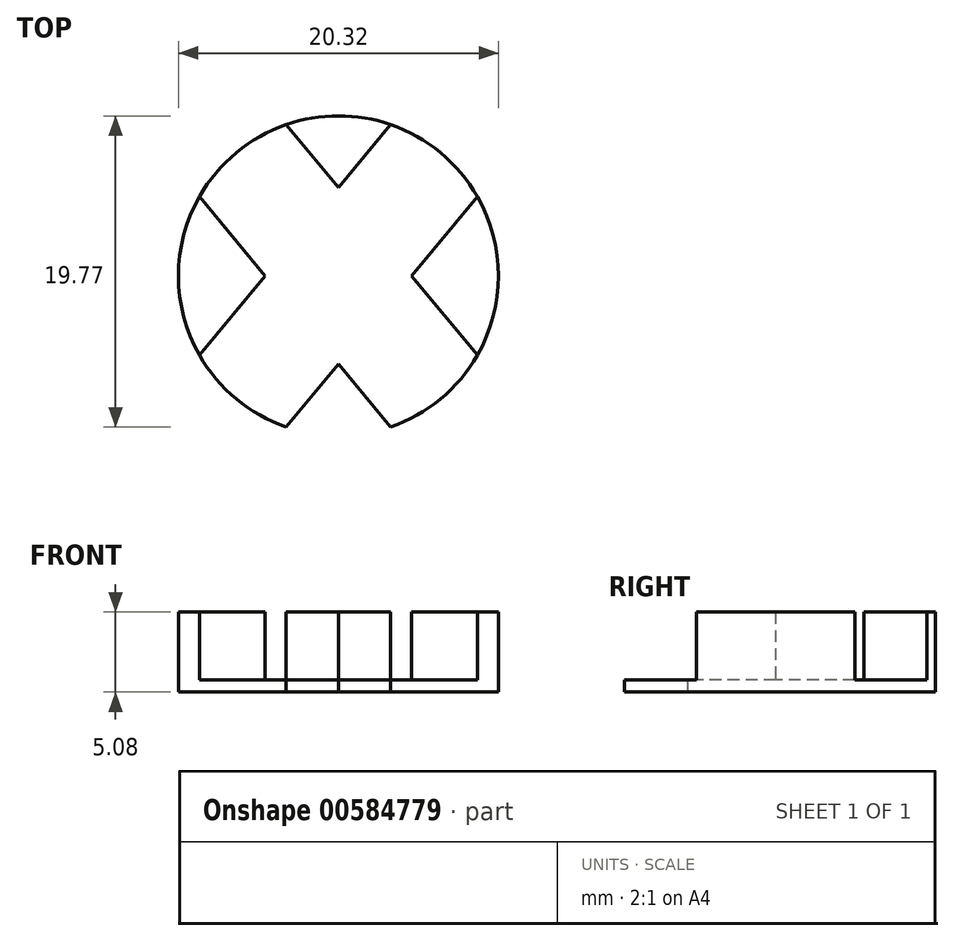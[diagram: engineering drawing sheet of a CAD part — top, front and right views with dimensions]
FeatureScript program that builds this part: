
annotation { "Feature Type Name" : "Feature", "Feature Type Description" : "" }
export const myFeature = defineFeature(function(context is Context, id is Id, definition is map)
    precondition{}
    {
        {
            var Q0;
            Q0=qCreatedBy(makeId("Top.planeOp"),FACE);
            var sketch = newSketch(context, id + "F0", { "sketchPlane" : qUnion([Q0])});
            skLineSegment(sketch, "E0", {"start": v(-47.75, 14) * mm, "end": v(-43.57, 8.97) * mm});
            skLineSegment(sketch, "E1", {"start": v(-30.1, 3.93) * mm, "end": v(-34.28, 8.97) * mm});
            skLineSegment(sketch, "E2", {"start": v(-35.6, 18.57) * mm, "end": v(-38.92, 14.57) * mm});
            skLineSegment(sketch, "E3", {"start": v(-42.24, -0.64) * mm, "end": v(-38.92, 3.36) * mm});
            skPoint(sketch, "E4.orphan", {"position": v(-38.92, 14.57) * mm});
            skArc(sketch, "E5", {"start": v(-42.24, -0.64) * mm, "mid": v(-38.92, 19.13) * mm, "end": v(-35.6, -0.64) * mm});
            skLineSegment(sketch, "E6.trimOffspring", {"start": v(-43.57, 8.97) * mm, "end": v(-47.75, 3.93) * mm});
            skLineSegment(sketch, "E7.trimOffspring", {"start": v(-38.92, 14.57) * mm, "end": v(-42.24, 18.57) * mm});
            skLineSegment(sketch, "E8.trimOffspring", {"start": v(-34.28, 8.97) * mm, "end": v(-30.1, 14) * mm});
            skLineSegment(sketch, "E9.trimOffspring", {"start": v(-38.92, 3.36) * mm, "end": v(-35.6, -0.64) * mm});
            skPoint(sketch, "E10.trimOffspring.start.orphan", {"position": v(-19.87, -19.6) * mm});
            skPoint(sketch, "E11.trimOffspring.end.orphan", {"position": v(-14.8, -19.6) * mm});
            skPoint(sketch, "E11.trimOffspring.start.orphan", {"position": v(-14.8, -14.53) * mm});
            skPoint(sketch, "E12.top.end.orphan", {"position": v(-57.97, -19.6) * mm});
            skPoint(sketch, "E13.trimOffspring.end.orphan", {"position": v(-63.05, -19.6) * mm});
            skPoint(sketch, "E13.trimOffspring.start.orphan", {"position": v(-63.05, -14.53) * mm});
            skPoint(sketch, "E12.left.end.orphan", {"position": v(-63.05, 32.46) * mm});
            skPoint(sketch, "E12.bottom.end.orphan", {"position": v(-57.97, 37.54) * mm});
            skPoint(sketch, "E12.bottom.start.orphan", {"position": v(-63.05, 37.54) * mm});
            skPoint(sketch, "E14.trimOffspring.start.orphan", {"position": v(-19.87, 37.54) * mm});
            skPoint(sketch, "E12.right.end.orphan", {"position": v(-14.8, 32.46) * mm});
            skPoint(sketch, "E12.right.start.orphan", {"position": v(-14.8, 37.54) * mm});
            skSolve(sketch);
        }
        {
            var Q0;
            {var subQ5=sQuery(id+"F0.wireOp",EDGE,"E0");Q0=makeQuery(id+"F0.imprint","IMPRINT",FACE,{"disambiguationData":[TD([[makeQuery(id+"F0.imprint","IMPRINT",EDGE,{"derivedFrom":subQ5}),1.0]])]});}
            extrude(context, id + "F1", {"entities" : qUnion([Q0]), "depth" : 0.76 * mm, "offsetDistance" : 25.4 * mm});
        }
        {
            var Q0;
            {var subQ0=sQuery(id+"F0.wireOp",EDGE,"E2");Q0=makeQuery(id+"F0.imprint","IMPRINT",FACE,{"disambiguationData":[TD([[makeQuery(id+"F0.imprint","IMPRINT",EDGE,{"derivedFrom":subQ0}),-1.0]])]});}
            var Q1;
            {var subQ0=sQuery(id+"F0.wireOp",EDGE,"E1");Q1=makeQuery(id+"F0.imprint","IMPRINT",FACE,{"disambiguationData":[TD([[makeQuery(id+"F0.imprint","IMPRINT",EDGE,{"derivedFrom":subQ0}),-1.0]])]});}
            var Q2;
            {var subQ0=sQuery(id+"F0.wireOp",EDGE,"E0");Q2=makeQuery(id+"F0.imprint","IMPRINT",FACE,{"disambiguationData":[TD([[makeQuery(id+"F0.imprint","IMPRINT",EDGE,{"derivedFrom":subQ0}),-1.0]])]});}
            extrude(context, id + "F2", {"entities" : qUnion([Q0, Q1, Q2]), "operationType" : NewBodyOperationType.ADD, "depth" : 5.08 * mm, "offsetDistance" : 25.4 * mm});
        }
    });
